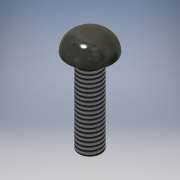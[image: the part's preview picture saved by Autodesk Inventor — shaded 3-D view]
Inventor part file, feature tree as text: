
AUTODESK INVENTOR PART (.ipt)
format: ipt  version: 2016 (Build 200138000, 138)  size: 148,480 bytes
history: native  units: mm
features: extrude x3, sketch x3, other x1, fillet x1, thread x1
ambient origin geometry x1: Origin
bodies: Body1 (feature_tree)
feature tree (9):
  other  "ソリッド1"
  extrude  "押し出し1"  Depth=4.0mm
  extrude  "押し出し2"  Depth=6.0mm TaperAngle=0.0deg
  fillet  "フィレット1"  Radius=8.0mm
  thread  "ねじ1"
  extrude  "押し出し3"  Depth=3.0mm TaperAngle=0.0deg
  sketch  "スケッチ1"
  sketch  "スケッチ2"
  sketch  "スケッチ3"
